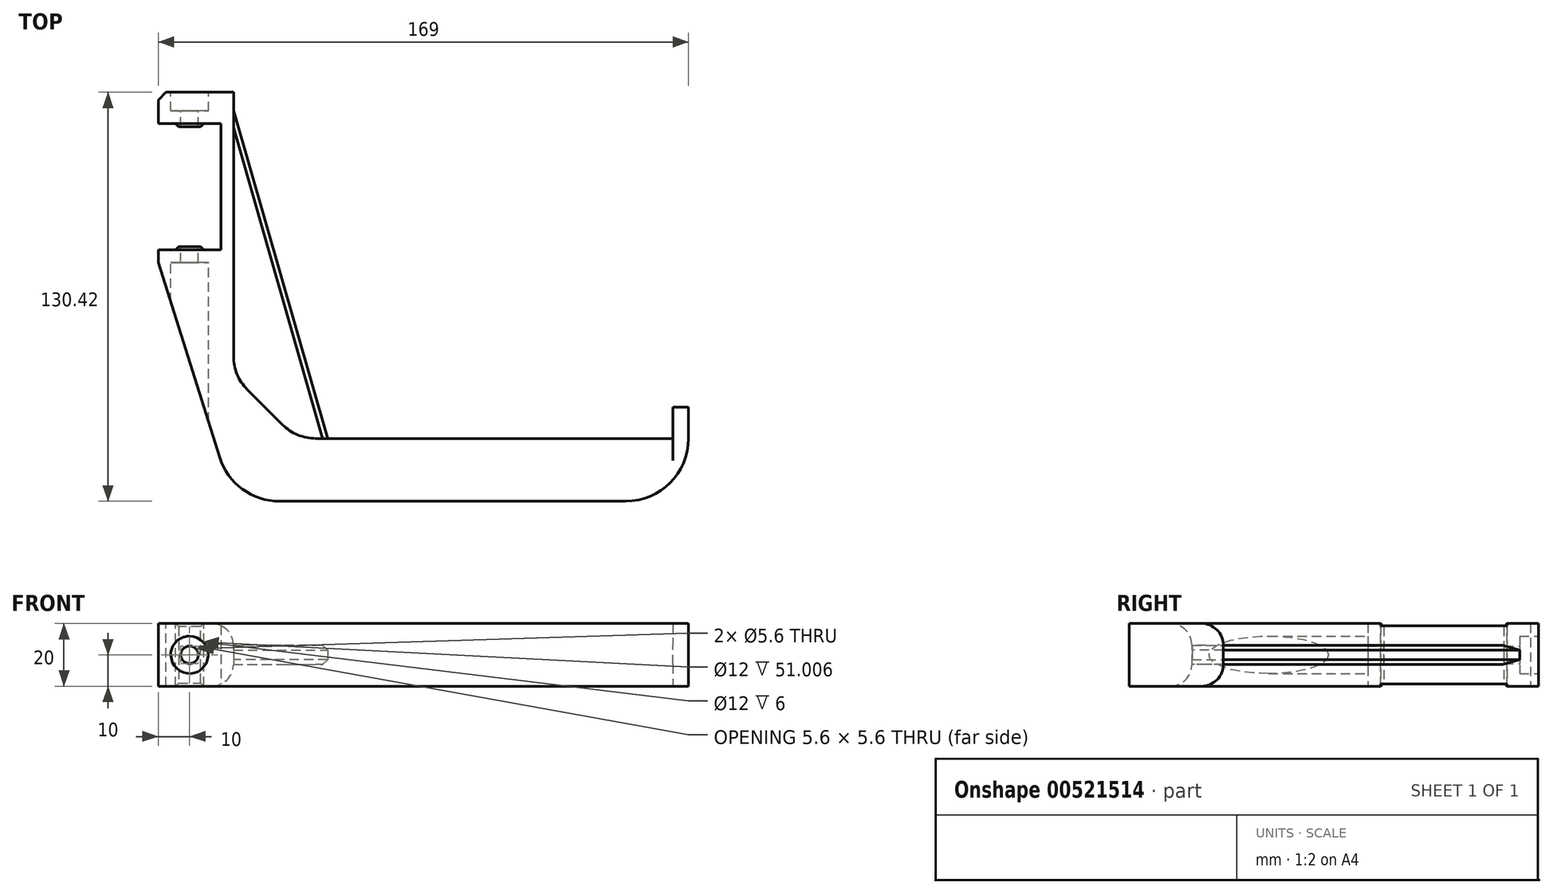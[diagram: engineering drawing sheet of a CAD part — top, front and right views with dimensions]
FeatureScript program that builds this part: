
annotation { "Feature Type Name" : "Feature", "Feature Type Description" : "" }
export const myFeature = defineFeature(function(context is Context, id is Id, definition is map)
    precondition{}
    {
        {
            var Q0;
            Q0=qCreatedBy(makeId("Top.planeOp"),FACE);
            var sketch = newSketch(context, id + "F0", { "sketchPlane" : qUnion([Q0])});
            skLineSegment(sketch, "E0", {"start": v(0, 0) * mm, "end": v(24, 0) * mm});
            skLineSegment(sketch, "E1", {"start": v(24, 0) * mm, "end": v(24, -48.3) * mm});
            skLineSegment(sketch, "E2", {"start": v(24, -48.3) * mm, "end": v(0, -48.3) * mm});
            skLineSegment(sketch, "E3", {"start": v(0, -48.3) * mm, "end": v(0, -44.3) * mm});
            skLineSegment(sketch, "E4", {"start": v(0, -44.3) * mm, "end": v(20, -44.3) * mm});
            skLineSegment(sketch, "E5", {"start": v(20, -44.3) * mm, "end": v(20, -4) * mm});
            skLineSegment(sketch, "E6", {"start": v(20, -4) * mm, "end": v(0, -4) * mm});
            skLineSegment(sketch, "E7", {"start": v(0, -4) * mm, "end": v(0, 0) * mm});
            skSolve(sketch);
        }
        {
            var Q0;
            Q0 = qSketchRegion(id + "F0", true);
            extrude(context, id + "F1", {"entities" : qUnion([Q0]), "depth" : 20 * mm, "offsetDistance" : 25 * mm});
        }
        {
            var Q0;
            Q0=makeQuery(id+"F1.opExtrude","CAP_FACE",FACE,{"disambiguationData":[OSD([sQuery(id+"F0.wireOp",EDGE,"E0"),sQuery(id+"F0.wireOp",EDGE,"E1"),sQuery(id+"F0.wireOp",EDGE,"E2"),sQuery(id+"F0.wireOp",EDGE,"E3"),sQuery(id+"F0.wireOp",EDGE,"E4"),sQuery(id+"F0.wireOp",EDGE,"E5"),sQuery(id+"F0.wireOp",EDGE,"E6"),sQuery(id+"F0.wireOp",EDGE,"E7")])],"isStart":false});
            var sketch = newSketch(context, id + "F2", { "sketchPlane" : qUnion([Q0])});
            skLineSegment(sketch, "E8.bottom", {"start": v(5.5, -4) * mm, "end": v(14.5, -4) * mm});
            skLineSegment(sketch, "E8.top", {"start": v(5.5, -5) * mm, "end": v(14.5, -5) * mm});
            skLineSegment(sketch, "E8.left", {"start": v(5.5, -4) * mm, "end": v(5.5, -5) * mm});
            skLineSegment(sketch, "E8.right", {"start": v(14.5, -4) * mm, "end": v(14.5, -5) * mm});
            skLineSegment(sketch, "E9.bottom", {"start": v(5.5, -44.3) * mm, "end": v(14.5, -44.3) * mm});
            skLineSegment(sketch, "E9.top", {"start": v(5.5, -43.3) * mm, "end": v(14.5, -43.3) * mm});
            skLineSegment(sketch, "E9.left", {"start": v(5.5, -44.3) * mm, "end": v(5.5, -43.3) * mm});
            skLineSegment(sketch, "E9.right", {"start": v(14.5, -44.3) * mm, "end": v(14.5, -43.3) * mm});
            skSolve(sketch);
        }
        {
            var Q0;
            Q0 = qSketchRegion(id + "F2", true);
            var Q1;
            Q1=makeQuery(id+"F1.opExtrude","CAP_FACE",FACE,{"disambiguationData":[OSD([sQuery(id+"F0.wireOp",EDGE,"E0"),sQuery(id+"F0.wireOp",EDGE,"E1"),sQuery(id+"F0.wireOp",EDGE,"E2"),sQuery(id+"F0.wireOp",EDGE,"E3"),sQuery(id+"F0.wireOp",EDGE,"E4"),sQuery(id+"F0.wireOp",EDGE,"E5"),sQuery(id+"F0.wireOp",EDGE,"E6"),sQuery(id+"F0.wireOp",EDGE,"E7")])],"isStart":true});
            extrude(context, id + "F3", {"entities" : qUnion([Q0]), "operationType" : NewBodyOperationType.ADD, "endBound" : BoundingType.UP_TO_SURFACE, "oppositeDirection" : true, "depth" : 25 * mm, "endBoundEntityFace" : qUnion([Q1]), "offsetDistance" : 25 * mm});
        }
        {
            var Q0;
            Q0=makeQuery(id+"F3.opExtrude","SWEPT_FACE",FACE,{"disambiguationData":[OSD([sQuery(id+"F2.wireOp",EDGE,"E8.top")])]});
            var Q1;
            Q1=makeQuery(id+"F3.opExtrude","SWEPT_FACE",FACE,{"disambiguationData":[OSD([sQuery(id+"F2.wireOp",EDGE,"E9.top")])]});
            chamfer(context, id + "F4", {"entities" : qUnion([Q0, Q1]), "width" : 1 * mm, "tangentPropagation" : true});
        }
        {
            var Q0;
            Q0=makeQuery(id+"F3.boolean.opBoolean","MERGE",FACE,{"derivedFrom":[makeQuery(id+"F1.opExtrude","CAP_FACE",FACE,{"disambiguationData":[OSD([sQuery(id+"F0.wireOp",EDGE,"E0"),sQuery(id+"F0.wireOp",EDGE,"E1"),sQuery(id+"F0.wireOp",EDGE,"E2"),sQuery(id+"F0.wireOp",EDGE,"E3"),sQuery(id+"F0.wireOp",EDGE,"E4"),sQuery(id+"F0.wireOp",EDGE,"E5"),sQuery(id+"F0.wireOp",EDGE,"E6"),sQuery(id+"F0.wireOp",EDGE,"E7")])],"isStart":false}),makeQuery(id+"F3.opExtrude","CAP_FACE",FACE,{"disambiguationData":[OSD([sQuery(id+"F2.wireOp",EDGE,"E8.bottom"),sQuery(id+"F2.wireOp",EDGE,"E8.top"),sQuery(id+"F2.wireOp",EDGE,"E8.left"),sQuery(id+"F2.wireOp",EDGE,"E8.right")])],"isStart":true}),makeQuery(id+"F3.opExtrude","CAP_FACE",FACE,{"disambiguationData":[OSD([sQuery(id+"F2.wireOp",EDGE,"E9.bottom"),sQuery(id+"F2.wireOp",EDGE,"E9.top"),sQuery(id+"F2.wireOp",EDGE,"E9.left"),sQuery(id+"F2.wireOp",EDGE,"E9.right")])],"isStart":true})]});
            var sketch = newSketch(context, id + "F5", { "sketchPlane" : qUnion([Q0])});
            skLineSegment(sketch, "E10", {"start": v(0, -48.3) * mm, "end": v(24, -124.42) * mm});
            skLineSegment(sketch, "E11", {"start": v(24, -124.42) * mm, "end": v(169, -124.42) * mm});
            skLineSegment(sketch, "E12", {"start": v(169, -124.42) * mm, "end": v(169, -94.42) * mm});
            skLineSegment(sketch, "E13", {"start": v(169, -94.42) * mm, "end": v(164, -94.42) * mm});
            skLineSegment(sketch, "E14", {"start": v(164, -94.42) * mm, "end": v(164, -104.42) * mm});
            skLineSegment(sketch, "E15", {"start": v(164, -104.42) * mm, "end": v(24, -104.42) * mm});
            skLineSegment(sketch, "E16", {"start": v(24, -48.3) * mm, "end": v(0, -48.3) * mm});
            skLineSegment(sketch, "E17", {"start": v(24, -48.3) * mm, "end": v(24, -104.42) * mm});
            skSolve(sketch);
        }
        {
            var Q0;
            Q0 = qSketchRegion(id + "F5", true);
            var Q1;
            Q1=makeQuery(id+"F3.boolean.opBoolean","MERGE",FACE,{"derivedFrom":[makeQuery(id+"F1.opExtrude","CAP_FACE",FACE,{"disambiguationData":[OSD([sQuery(id+"F0.wireOp",EDGE,"E0"),sQuery(id+"F0.wireOp",EDGE,"E1"),sQuery(id+"F0.wireOp",EDGE,"E2"),sQuery(id+"F0.wireOp",EDGE,"E3"),sQuery(id+"F0.wireOp",EDGE,"E4"),sQuery(id+"F0.wireOp",EDGE,"E5"),sQuery(id+"F0.wireOp",EDGE,"E6"),sQuery(id+"F0.wireOp",EDGE,"E7")])],"isStart":true}),makeQuery(id+"F3.opExtrude","CAP_FACE",FACE,{"disambiguationData":[OSD([sQuery(id+"F2.wireOp",EDGE,"E8.bottom"),sQuery(id+"F2.wireOp",EDGE,"E8.top"),sQuery(id+"F2.wireOp",EDGE,"E8.left"),sQuery(id+"F2.wireOp",EDGE,"E8.right")])],"isStart":false}),makeQuery(id+"F3.opExtrude","CAP_FACE",FACE,{"disambiguationData":[OSD([sQuery(id+"F2.wireOp",EDGE,"E9.bottom"),sQuery(id+"F2.wireOp",EDGE,"E9.top"),sQuery(id+"F2.wireOp",EDGE,"E9.left"),sQuery(id+"F2.wireOp",EDGE,"E9.right")])],"isStart":false})]});
            extrude(context, id + "F6", {"entities" : qUnion([Q0]), "operationType" : NewBodyOperationType.ADD, "endBound" : BoundingType.UP_TO_SURFACE, "oppositeDirection" : true, "depth" : 25 * mm, "endBoundEntityFace" : qUnion([Q1]), "offsetDistance" : 25 * mm});
        }
        {
            var Q0;
            Q0=makeQuery(id+"F6.boolean.opBoolean","MERGE",FACE,{"derivedFrom":[makeQuery(id+"F3.boolean.opBoolean","MERGE",FACE,{"derivedFrom":[makeQuery(id+"F1.opExtrude","CAP_FACE",FACE,{"disambiguationData":[OSD([sQuery(id+"F0.wireOp",EDGE,"E0"),sQuery(id+"F0.wireOp",EDGE,"E1"),sQuery(id+"F0.wireOp",EDGE,"E2"),sQuery(id+"F0.wireOp",EDGE,"E3"),sQuery(id+"F0.wireOp",EDGE,"E4"),sQuery(id+"F0.wireOp",EDGE,"E5"),sQuery(id+"F0.wireOp",EDGE,"E6"),sQuery(id+"F0.wireOp",EDGE,"E7")])],"isStart":false}),makeQuery(id+"F3.opExtrude","CAP_FACE",FACE,{"disambiguationData":[OSD([sQuery(id+"F2.wireOp",EDGE,"E8.bottom"),sQuery(id+"F2.wireOp",EDGE,"E8.top"),sQuery(id+"F2.wireOp",EDGE,"E8.left"),sQuery(id+"F2.wireOp",EDGE,"E8.right")])],"isStart":true}),makeQuery(id+"F3.opExtrude","CAP_FACE",FACE,{"disambiguationData":[OSD([sQuery(id+"F2.wireOp",EDGE,"E9.bottom"),sQuery(id+"F2.wireOp",EDGE,"E9.top"),sQuery(id+"F2.wireOp",EDGE,"E9.left"),sQuery(id+"F2.wireOp",EDGE,"E9.right")])],"isStart":true})]}),makeQuery(id+"F6.opExtrude","CAP_FACE",FACE,{"disambiguationData":[OSD([sQuery(id+"F5.wireOp",EDGE,"E10"),sQuery(id+"F5.wireOp",EDGE,"E11"),sQuery(id+"F5.wireOp",EDGE,"E12"),sQuery(id+"F5.wireOp",EDGE,"E13"),sQuery(id+"F5.wireOp",EDGE,"E14"),sQuery(id+"F5.wireOp",EDGE,"E15"),sQuery(id+"F5.wireOp",EDGE,"E16"),sQuery(id+"F5.wireOp",EDGE,"E17")])],"isStart":true})]});
            cPlane(context, id + "F7", {"entities" : qUnion([Q0]), "cplaneType" : CPlaneType.OFFSET, "offset" : 10 * mm, "oppositeDirection" : true, "width" : 150 * mm, "height" : 150 * mm});
        }
        {
            var Q0;
            Q0=qCreatedBy(id+"F7.planeOp",FACE);
            var sketch = newSketch(context, id + "F8", { "sketchPlane" : qUnion([Q0])});
            skLineSegment(sketch, "E18.0.0", {"start": v(20, -44.3) * mm, "end": v(14.5, -44.3) * mm, "construction": true});
            skLineSegment(sketch, "E18.0.1", {"start": v(14.5, -44.3) * mm, "end": v(5.5, -44.3) * mm, "construction": true});
            skLineSegment(sketch, "E18.0.2", {"start": v(5.5, -44.3) * mm, "end": v(0, -44.3) * mm, "construction": true});
            skLineSegment(sketch, "E18.0.3", {"start": v(0, -44.3) * mm, "end": v(0, -48.3) * mm, "construction": true});
            skLineSegment(sketch, "E18.0.4", {"start": v(0, -48.3) * mm, "end": v(24, -124.42) * mm, "construction": true});
            skLineSegment(sketch, "E18.0.5", {"start": v(24, -124.42) * mm, "end": v(169, -124.42) * mm, "construction": true});
            skLineSegment(sketch, "E18.0.6", {"start": v(169, -124.42) * mm, "end": v(169, -94.42) * mm, "construction": true});
            skLineSegment(sketch, "E18.0.7", {"start": v(169, -94.42) * mm, "end": v(164, -94.42) * mm, "construction": true});
            skLineSegment(sketch, "E18.0.8", {"start": v(164, -94.42) * mm, "end": v(164, -104.42) * mm, "construction": true});
            skLineSegment(sketch, "E18.0.9", {"start": v(164, -104.42) * mm, "end": v(24, -104.42) * mm, "construction": true});
            skLineSegment(sketch, "E18.0.10", {"start": v(24, -104.42) * mm, "end": v(24, 0) * mm, "construction": true});
            skLineSegment(sketch, "E18.0.11", {"start": v(24, 0) * mm, "end": v(0, 0) * mm, "construction": true});
            skLineSegment(sketch, "E18.0.12", {"start": v(0, 0) * mm, "end": v(0, -4) * mm, "construction": true});
            skLineSegment(sketch, "E18.0.13", {"start": v(0, -4) * mm, "end": v(5.5, -4) * mm, "construction": true});
            skLineSegment(sketch, "E18.0.14", {"start": v(5.5, -4) * mm, "end": v(14.5, -4) * mm, "construction": true});
            skLineSegment(sketch, "E18.0.15", {"start": v(14.5, -4) * mm, "end": v(20, -4) * mm, "construction": true});
            skLineSegment(sketch, "E18.0.16", {"start": v(20, -4) * mm, "end": v(20, -44.3) * mm, "construction": true});
            skLineSegment(sketch, "E19", {"start": v(24, 0) * mm, "end": v(54, -104.42) * mm});
            skLineSegment(sketch, "E20", {"start": v(54, -104.42) * mm, "end": v(24, -104.42) * mm});
            skLineSegment(sketch, "E21", {"start": v(24, -104.42) * mm, "end": v(24, 0) * mm});
            skSolve(sketch);
        }
        {
            var Q0;
            Q0 = qSketchRegion(id + "F8", true);
            extrude(context, id + "F9", {"entities" : qUnion([Q0]), "operationType" : NewBodyOperationType.ADD, "endBound" : BoundingType.SYMMETRIC, "depth" : 6 * mm, "offsetDistance" : 25 * mm});
        }
        {
            var Q0;
            {var subQ0=sQuery(id+"F5.wireOp",EDGE,"E17");var subQ2=sQuery(id+"F5.wireOp",EDGE,"E15");Q0=makeQuery(id+"F9.boolean.opBoolean","SPLIT",EDGE,{"disambiguationData":[TD([makeQuery(id+"F9.opExtrude","CAP_FACE",FACE,{"disambiguationData":[OSD([sQuery(id+"F8.wireOp",EDGE,"E19"),sQuery(id+"F8.wireOp",EDGE,"E20"),sQuery(id+"F8.wireOp",EDGE,"E21")])],"isStart":false})])],"derivedFrom":makeQuery(id+"F6.opExtrude","SWEPT_EDGE",EDGE,{"disambiguationData":[OSD([subQ2,subQ0])]})});}
            var Q1;
            {var subQ1=sQuery(id+"F5.wireOp",EDGE,"E17");var subQ2=sQuery(id+"F5.wireOp",EDGE,"E15");Q1=makeQuery(id+"F9.boolean.opBoolean","SPLIT",EDGE,{"disambiguationData":[TD([makeQuery(id+"F9.opExtrude","CAP_FACE",FACE,{"disambiguationData":[OSD([sQuery(id+"F8.wireOp",EDGE,"E19"),sQuery(id+"F8.wireOp",EDGE,"E20"),sQuery(id+"F8.wireOp",EDGE,"E21")])],"isStart":true})])],"derivedFrom":makeQuery(id+"F6.opExtrude","SWEPT_EDGE",EDGE,{"disambiguationData":[OSD([subQ2,subQ1])]})});}
            chamfer(context, id + "F10", {"entities" : qUnion([Q0, Q1]), "width" : 20 * mm, "tangentPropagation" : true});
        }
        {
            var Q0;
            Q0=makeQuery(id+"F1.opExtrude","SWEPT_FACE",FACE,{"disambiguationData":[OSD([sQuery(id+"F0.wireOp",EDGE,"E0")])]});
            extrude(context, id + "F11", {"entities" : qUnion([Q0]), "operationType" : NewBodyOperationType.ADD, "depth" : 6 * mm, "offsetDistance" : 25 * mm});
        }
        {
            var Q0;
            {var subQ7=sQuery(id+"F0.wireOp",EDGE,"E4");var subQ8=sQuery(id+"F0.wireOp",EDGE,"E3");Q0=makeQuery(id+"F3.boolean.opBoolean","SPLIT",FACE,{"disambiguationData":[TD([makeQuery(id+"F1.opExtrude","SWEPT_FACE",FACE,{"disambiguationData":[OSD([subQ8])]})])],"derivedFrom":makeQuery(id+"F1.opExtrude","SWEPT_FACE",FACE,{"disambiguationData":[OSD([subQ7])]})});}
            cPlane(context, id + "F12", {"entities" : qUnion([Q0]), "cplaneType" : CPlaneType.OFFSET, "offset" : 4 * mm, "oppositeDirection" : true, "width" : 150 * mm, "height" : 150 * mm});
        }
        {
            var Q0;
            Q0=makeQuery(id+"F11.opExtrude","CAP_FACE",FACE,{"disambiguationData":[OSD([sQuery(id+"F0.wireOp",EDGE,"E0")])],"isStart":false});
            var sketch = newSketch(context, id + "F13", { "sketchPlane" : qUnion([Q0])});
            skCircle(sketch, "E22", {"center": v(-10, 10) * mm, "radius": 2.8 * mm});
            skPoint(sketch, "E22.centerSnap0", {"position": v(0, 10) * mm});
            skPoint(sketch, "E22.centerSnap1", {"position": v(-12, 20) * mm});
            skSolve(sketch);
        }
        {
            var Q0;
            Q0 = qSketchRegion(id + "F13", true);
            extrude(context, id + "F14", {"entities" : qUnion([Q0]), "operationType" : NewBodyOperationType.REMOVE, "endBound" : BoundingType.THROUGH_ALL, "oppositeDirection" : true, "depth" : 25 * mm, "offsetDistance" : 25 * mm});
        }
        {
            var Q0;
            Q0=qCreatedBy(id+"F12.planeOp",FACE);
            var sketch = newSketch(context, id + "F15", { "sketchPlane" : qUnion([Q0])});
            skCircle(sketch, "E23.0", {"center": v(-10, 10) * mm, "radius": 2.8 * mm, "construction": true});
            skCircle(sketch, "E24", {"center": v(-10, 10) * mm, "radius": 6 * mm});
            skSolve(sketch);
        }
        {
            var Q0;
            Q0 = qSketchRegion(id + "F15", true);
            extrude(context, id + "F16", {"entities" : qUnion([Q0]), "operationType" : NewBodyOperationType.REMOVE, "endBound" : BoundingType.THROUGH_ALL, "oppositeDirection" : true, "depth" : 25 * mm, "offsetDistance" : 25 * mm});
        }
        {
            var Q0;
            Q0=makeQuery(id+"F11.opExtrude","CAP_FACE",FACE,{"disambiguationData":[OSD([sQuery(id+"F0.wireOp",EDGE,"E0")])],"isStart":false});
            var sketch = newSketch(context, id + "F17", { "sketchPlane" : qUnion([Q0])});
            skCircle(sketch, "E25", {"center": v(-10, 10) * mm, "radius": 6 * mm});
            skSolve(sketch);
        }
        {
            var Q0;
            Q0 = qSketchRegion(id + "F17", true);
            extrude(context, id + "F18", {"entities" : qUnion([Q0]), "operationType" : NewBodyOperationType.REMOVE, "oppositeDirection" : true, "depth" : 6 * mm, "offsetDistance" : 25 * mm});
        }
        {
            var Q0;
            {var subQ0=sQuery(id+"F5.wireOp",EDGE,"E15");var subQ1=makeQuery(id+"F6.opExtrude","SWEPT_FACE",FACE,{"disambiguationData":[OSD([subQ0])]});var subQ3=sQuery(id+"F5.wireOp",EDGE,"E17");Q0=makeQuery(id+"F10.opChamfer","BLEND_EDGE",EDGE,{"blendedFrom":[makeQuery(id+"F9.boolean.opBoolean","SPLIT",EDGE,{"disambiguationData":[TD([makeQuery(id+"F9.opExtrude","CAP_FACE",FACE,{"disambiguationData":[OSD([sQuery(id+"F8.wireOp",EDGE,"E19"),sQuery(id+"F8.wireOp",EDGE,"E20"),sQuery(id+"F8.wireOp",EDGE,"E21")])],"isStart":true})])],"derivedFrom":makeQuery(id+"F6.opExtrude","SWEPT_EDGE",EDGE,{"disambiguationData":[OSD([subQ0,subQ3])]})}),subQ1],"blendedInto":[subQ1]});}
            var Q1;
            {var subQ1=sQuery(id+"F8.wireOp",EDGE,"E19");var subQ2=makeQuery(id+"F9.opExtrude","CAP_FACE",FACE,{"disambiguationData":[OSD([subQ1,sQuery(id+"F8.wireOp",EDGE,"E20"),sQuery(id+"F8.wireOp",EDGE,"E21")])],"isStart":true});var subQ3=sQuery(id+"F0.wireOp",EDGE,"E1");var subQ6=sQuery(id+"F5.wireOp",EDGE,"E17");var subQ7=sQuery(id+"F5.wireOp",EDGE,"E15");var subQ11=makeQuery(id+"F6.opExtrude","SWEPT_FACE",FACE,{"disambiguationData":[OSD([subQ6])]});var subQ12=makeQuery(id+"F1.opExtrude","SWEPT_FACE",FACE,{"disambiguationData":[OSD([subQ3])]});Q1=makeQuery(id+"F10.opChamfer","BLEND_EDGE",EDGE,{"blendedFrom":[makeQuery(id+"F9.boolean.opBoolean","SPLIT",EDGE,{"disambiguationData":[TD([subQ2])],"derivedFrom":makeQuery(id+"F6.opExtrude","SWEPT_EDGE",EDGE,{"disambiguationData":[OSD([subQ7,subQ6])]})}),makeQuery(id+"F9.boolean.opBoolean","SPLIT",FACE,{"disambiguationData":[TD([subQ2])],"derivedFrom":makeQuery(id+"F6.boolean.opBoolean","MERGE",FACE,{"derivedFrom":[subQ12,subQ11]})})],"blendedInto":[makeQuery(id+"F9.boolean.opBoolean","SPLIT",FACE,{"disambiguationData":[TD([subQ2])],"derivedFrom":makeQuery(id+"F6.boolean.opBoolean","MERGE",FACE,{"derivedFrom":[subQ12,subQ11]})})]});}
            var Q2;
            {var subQ1=sQuery(id+"F0.wireOp",EDGE,"E1");var subQ5=sQuery(id+"F8.wireOp",EDGE,"E19");var subQ6=sQuery(id+"F5.wireOp",EDGE,"E17");var subQ7=sQuery(id+"F5.wireOp",EDGE,"E15");var subQ10=makeQuery(id+"F9.opExtrude","CAP_FACE",FACE,{"disambiguationData":[OSD([subQ5,sQuery(id+"F8.wireOp",EDGE,"E20"),sQuery(id+"F8.wireOp",EDGE,"E21")])],"isStart":false});var subQ11=makeQuery(id+"F6.opExtrude","SWEPT_FACE",FACE,{"disambiguationData":[OSD([subQ6])]});var subQ12=makeQuery(id+"F1.opExtrude","SWEPT_FACE",FACE,{"disambiguationData":[OSD([subQ1])]});Q2=makeQuery(id+"F10.opChamfer","BLEND_EDGE",EDGE,{"blendedFrom":[makeQuery(id+"F9.boolean.opBoolean","SPLIT",EDGE,{"disambiguationData":[TD([subQ10])],"derivedFrom":makeQuery(id+"F6.opExtrude","SWEPT_EDGE",EDGE,{"disambiguationData":[OSD([subQ7,subQ6])]})}),makeQuery(id+"F9.boolean.opBoolean","SPLIT",FACE,{"disambiguationData":[TD([subQ10])],"derivedFrom":makeQuery(id+"F6.boolean.opBoolean","MERGE",FACE,{"derivedFrom":[subQ12,subQ11]})})],"blendedInto":[makeQuery(id+"F9.boolean.opBoolean","SPLIT",FACE,{"disambiguationData":[TD([subQ10])],"derivedFrom":makeQuery(id+"F6.boolean.opBoolean","MERGE",FACE,{"derivedFrom":[subQ12,subQ11]})})]});}
            var Q3;
            {var subQ0=sQuery(id+"F5.wireOp",EDGE,"E15");var subQ1=makeQuery(id+"F6.opExtrude","SWEPT_FACE",FACE,{"disambiguationData":[OSD([subQ0])]});var subQ2=sQuery(id+"F5.wireOp",EDGE,"E17");Q3=makeQuery(id+"F10.opChamfer","BLEND_EDGE",EDGE,{"blendedFrom":[makeQuery(id+"F9.boolean.opBoolean","SPLIT",EDGE,{"disambiguationData":[TD([makeQuery(id+"F9.opExtrude","CAP_FACE",FACE,{"disambiguationData":[OSD([sQuery(id+"F8.wireOp",EDGE,"E19"),sQuery(id+"F8.wireOp",EDGE,"E20"),sQuery(id+"F8.wireOp",EDGE,"E21")])],"isStart":false})])],"derivedFrom":makeQuery(id+"F6.opExtrude","SWEPT_EDGE",EDGE,{"disambiguationData":[OSD([subQ0,subQ2])]})}),subQ1],"blendedInto":[subQ1]});}
            fillet(context, id + "F19", {"entities" : qUnion([Q0, Q1, Q2, Q3]), "radius" : 15 * mm, "tangentPropagation" : true, "allowEdgeOverflow" : false});
        }
        {
            var Q0;
            Q0=makeQuery(id+"F6.opExtrude","CAP_EDGE",EDGE,{"disambiguationData":[OSD([sQuery(id+"F5.wireOp",EDGE,"E15")])],"isStart":true});
            var Q1;
            Q1=makeQuery(id+"F6.opExtrude","CAP_EDGE",EDGE,{"disambiguationData":[OSD([sQuery(id+"F5.wireOp",EDGE,"E15")])],"isStart":false});
            var Q2;
            Q2=makeQuery(id+"F6.opExtrude","CAP_EDGE",EDGE,{"disambiguationData":[OSD([sQuery(id+"F5.wireOp",EDGE,"E13")])],"isStart":false});
            var Q3;
            Q3=makeQuery(id+"F6.opExtrude","CAP_EDGE",EDGE,{"disambiguationData":[OSD([sQuery(id+"F5.wireOp",EDGE,"E13")])],"isStart":true});
            fillet(context, id + "F20", {"entities" : qUnion([Q0, Q1, Q2, Q3]), "radius" : 7 * mm, "tangentPropagation" : true, "allowEdgeOverflow" : false});
        }
        {
            var Q0;
            Q0=makeQuery(id+"F9.opExtrude","CAP_EDGE",EDGE,{"disambiguationData":[OSD([sQuery(id+"F8.wireOp",EDGE,"E19")])],"isStart":false});
            var Q1;
            Q1=makeQuery(id+"F9.opExtrude","CAP_EDGE",EDGE,{"disambiguationData":[OSD([sQuery(id+"F8.wireOp",EDGE,"E19")])],"isStart":true});
            chamfer(context, id + "F21", {"entities" : qUnion([Q0, Q1]), "width" : 1.5 * mm, "tangentPropagation" : true});
        }
        {
            var Q0;
            Q0=makeQuery(id+"F6.opExtrude","SWEPT_EDGE",EDGE,{"disambiguationData":[OSD([sQuery(id+"F5.wireOp",EDGE,"E10"),sQuery(id+"F5.wireOp",EDGE,"E11")])]});
            var Q1;
            Q1=makeQuery(id+"F6.opExtrude","SWEPT_EDGE",EDGE,{"disambiguationData":[OSD([sQuery(id+"F5.wireOp",EDGE,"E11"),sQuery(id+"F5.wireOp",EDGE,"E12")])]});
            fillet(context, id + "F22", {"entities" : qUnion([Q0, Q1]), "radius" : 20 * mm, "tangentPropagation" : true, "allowEdgeOverflow" : false});
        }
        {
            var Q0;
            Q0=makeQuery(id+"F11.opExtrude","CAP_EDGE",EDGE,{"disambiguationData":[OSD([sQuery(id+"F0.wireOp",EDGE,"E0"),sQuery(id+"F0.wireOp",EDGE,"E7")])],"isStart":false});
            chamfer(context, id + "F23", {"entities" : qUnion([Q0]), "width" : 2.5 * mm, "tangentPropagation" : true});
        }
    });
